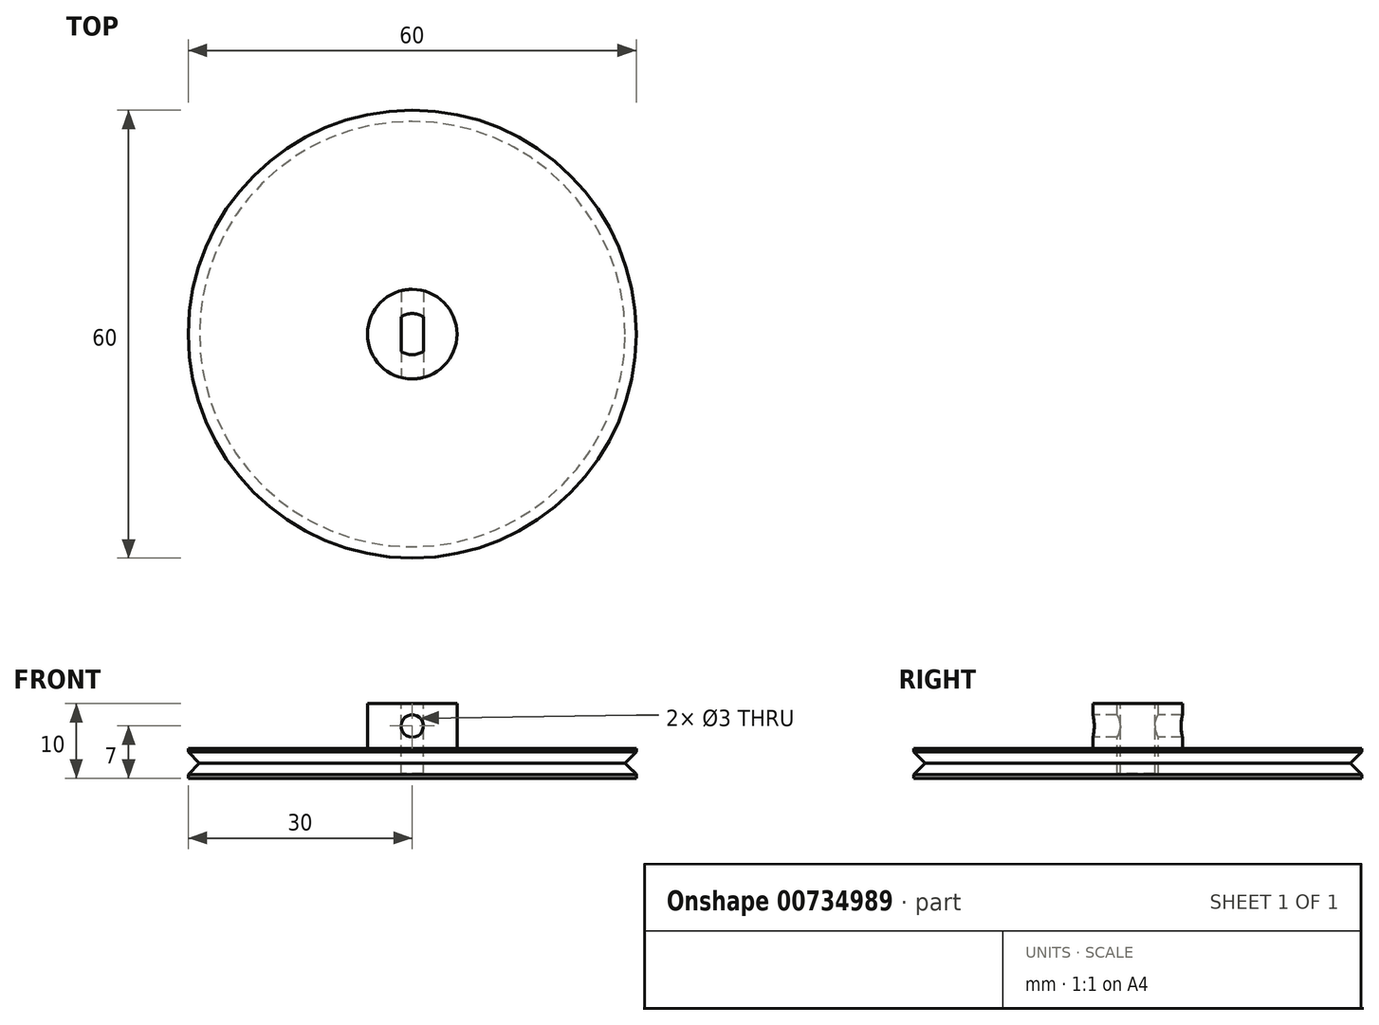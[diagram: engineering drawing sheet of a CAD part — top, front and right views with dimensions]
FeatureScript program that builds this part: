
annotation { "Feature Type Name" : "Feature", "Feature Type Description" : "" }
export const myFeature = defineFeature(function(context is Context, id is Id, definition is map)
    precondition{}
    {
        {
            var Q0;
            Q0=qCreatedBy(makeId("Top.planeOp"),FACE);
            var sketch = newSketch(context, id + "F0", { "sketchPlane" : qUnion([Q0])});
            skCircle(sketch, "E0", {"center": v(0, 0) * mm, "radius": 30 * mm});
            skCircle(sketch, "E1", {"center": v(0, 0) * mm, "radius": 6 * mm});
            skSolve(sketch);
        }
        {
            var Q0;
            Q0 = qSketchRegion(id + "F0", true);
            var Q1;
            Q1=makeQuery(id+"F0.imprint","IMPRINT",FACE,{"disambiguationData":[TD([[makeQuery(id+"F0.imprint","IMPRINT",EDGE,{"derivedFrom":sQuery(id+"F0.wireOp",EDGE,"E1")}),1.0]])]});
            extrude(context, id + "F1", {"entities" : qUnion([Q0, Q1]), "oppositeDirection" : true, "depth" : 4 * mm, "offsetDistance" : 25 * mm});
        }
        {
            var Q0;
            Q0=makeQuery(id+"F0.imprint","IMPRINT",FACE,{"disambiguationData":[TD([[makeQuery(id+"F0.imprint","IMPRINT",EDGE,{"derivedFrom":sQuery(id+"F0.wireOp",EDGE,"E1")}),1.0]])]});
            extrude(context, id + "F2", {"entities" : qUnion([Q0]), "operationType" : NewBodyOperationType.ADD, "depth" : 6 * mm, "offsetDistance" : 25 * mm});
        }
        {
            var Q0;
            Q0=qCreatedBy(makeId("Front.planeOp"),FACE);
            var sketch = newSketch(context, id + "F3", { "sketchPlane" : qUnion([Q0])});
            skCircle(sketch, "E2", {"center": v(0, 3) * mm, "radius": 1.5 * mm});
            skSolve(sketch);
        }
        {
            var Q0;
            Q0 = qSketchRegion(id + "F3", true);
            extrude(context, id + "F4", {"entities" : qUnion([Q0]), "operationType" : NewBodyOperationType.REMOVE, "endBound" : BoundingType.SYMMETRIC, "oppositeDirection" : true, "depth" : 25 * mm, "offsetDistance" : 25 * mm});
        }
        {
            var Q0;
            Q0=makeQuery(id+"F2.opExtrude","CAP_FACE",FACE,{"disambiguationData":[OSD([sQuery(id+"F0.wireOp",EDGE,"E1")])],"isStart":false});
            var sketch = newSketch(context, id + "F5", { "sketchPlane" : qUnion([Q0])});
            skLineSegment(sketch, "E3.bottom", {"start": v(-1.5, 2.3) * mm, "end": v(1.5, 2.3) * mm});
            skLineSegment(sketch, "E3.top", {"start": v(-1.5, -2.3) * mm, "end": v(1.5, -2.3) * mm});
            skLineSegment(sketch, "E3.left", {"start": v(-1.5, 2.3) * mm, "end": v(-1.5, -2.3) * mm});
            skLineSegment(sketch, "E3.right", {"start": v(1.5, 2.3) * mm, "end": v(1.5, -2.3) * mm});
            skPoint(sketch, "E3.middle", {"position": v(0, 0) * mm});
            skArc(sketch, "E4", {"start": v(1.5, 2.3) * mm, "mid": v(0, 2.75) * mm, "end": v(-1.5, 2.3) * mm});
            skArc(sketch, "E5", {"start": v(-1.5, -2.3) * mm, "mid": v(0, -2.75) * mm, "end": v(1.5, -2.3) * mm});
            skSolve(sketch);
        }
        {
            var Q0;
            Q0 = qSketchRegion(id + "F5", true);
            extrude(context, id + "F6", {"entities" : qUnion([Q0]), "operationType" : NewBodyOperationType.REMOVE, "oppositeDirection" : true, "depth" : 9.4 * mm, "offsetDistance" : 25 * mm});
        }
        {
            var Q0;
            Q0=qCreatedBy(makeId("Front.planeOp"),FACE);
            var sketch = newSketch(context, id + "F7", { "sketchPlane" : qUnion([Q0])});
            skLineSegment(sketch, "E6", {"start": v(30, 0) * mm, "end": v(30, -4) * mm, "construction": true});
            skLineSegment(sketch, "E7", {"start": v(30, -0.48) * mm, "end": v(28.5, -1.98) * mm});
            skLineSegment(sketch, "E8", {"start": v(28.5, -1.98) * mm, "end": v(30, -3.48) * mm});
            skLineSegment(sketch, "E9", {"start": v(30, -2) * mm, "end": v(26.78, -2) * mm, "construction": true});
            skLineSegment(sketch, "E10", {"start": v(30, -0.48) * mm, "end": v(30, -3.48) * mm});
            skLineSegment(sketch, "E11", {"start": v(0, 8.92) * mm, "end": v(0, -9.76) * mm, "construction": true});
            skSolve(sketch);
        }
        {
            var Q0;
            Q0 = qSketchRegion(id + "F7", true);
            var Q1;
            Q1=sQuery(id+"F7.wireOp",EDGE,"E11");
            revolve(context, id + "F8", {"operationType" : NewBodyOperationType.REMOVE, "surfaceOperationType" : NewSurfaceOperationType.NEW, "entities" : qUnion([Q0]), "axis" : qUnion([Q1]), "revolveType" : RevolveType.FULL});
        }
    });
